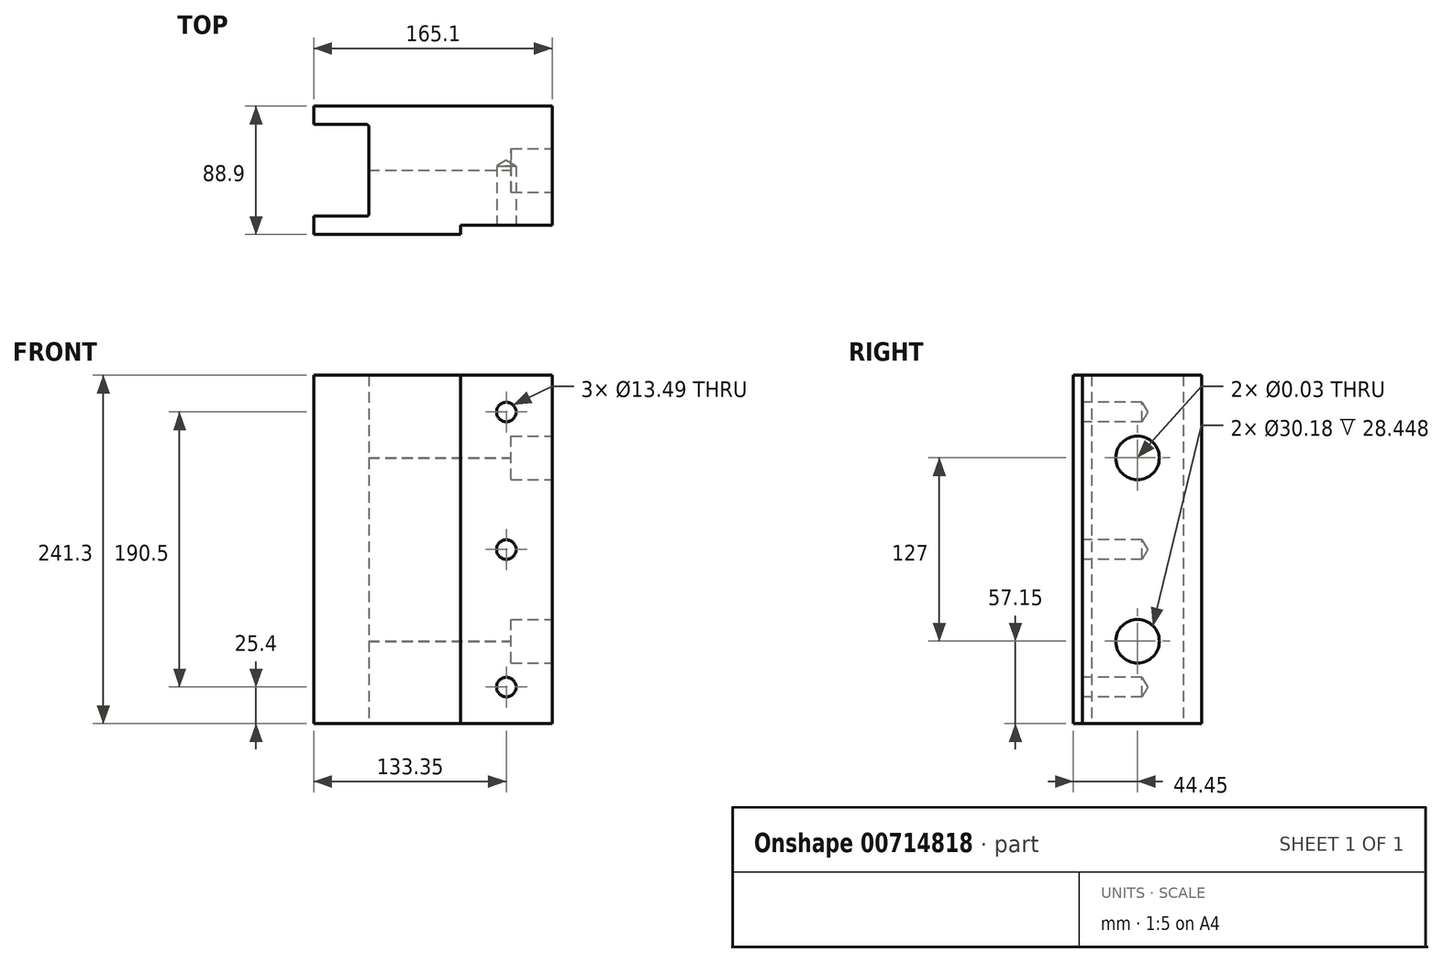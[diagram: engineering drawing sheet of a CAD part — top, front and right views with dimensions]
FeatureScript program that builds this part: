
annotation { "Feature Type Name" : "Feature", "Feature Type Description" : "" }
export const myFeature = defineFeature(function(context is Context, id is Id, definition is map)
    precondition{}
    {
        {
            var Q0;
            Q0=qCreatedBy(makeId("Top.planeOp"),FACE);
            var sketch = newSketch(context, id + "F0", { "sketchPlane" : qUnion([Q0])});
            skLineSegment(sketch, "E0.bottom", {"start": v(-82.55, 44.45) * mm, "end": v(82.55, 44.45) * mm});
            skLineSegment(sketch, "E0.top", {"start": v(-82.55, -44.45) * mm, "end": v(82.55, -44.45) * mm});
            skLineSegment(sketch, "E0.left", {"start": v(-82.55, 44.45) * mm, "end": v(-82.55, 31.75) * mm});
            skLineSegment(sketch, "E0.right", {"start": v(82.55, 44.45) * mm, "end": v(82.55, -44.45) * mm});
            skPoint(sketch, "E0.middle", {"position": v(0, 0) * mm});
            skLineSegment(sketch, "E1.bottom", {"start": v(-44.45, -31.75) * mm, "end": v(-120.65, -31.75) * mm});
            skLineSegment(sketch, "E1.top", {"start": v(-44.45, 31.75) * mm, "end": v(-120.65, 31.75) * mm});
            skLineSegment(sketch, "E1.left", {"start": v(-44.45, -31.75) * mm, "end": v(-44.45, 31.75) * mm});
            skPoint(sketch, "E1.middle", {"position": v(-82.55, 0) * mm});
            skLineSegment(sketch, "E2.trimOffspring", {"start": v(-82.55, 0) * mm, "end": v(-82.55, -44.45) * mm});
            skSolve(sketch);
        }
        {
            var Q0;
            Q0=qSketchRegion(id+"F0",true);
            extrude(context, id + "F1", {"entities" : qUnion([Q0]), "endBound" : BoundingType.SYMMETRIC, "depth" : 241.3 * mm, "offsetDistance" : 25.4 * mm});
        }
        {
            var Q0;
            Q0=makeQuery(id+"F1.opExtrude","SWEPT_EDGE",EDGE,{"disambiguationData":[OSD([sQuery(id+"F0.wireOp",EDGE,"E1.top"),sQuery(id+"F0.wireOp",EDGE,"E1.left")])]});
            var Q1;
            Q1=makeQuery(id+"F1.opExtrude","SWEPT_EDGE",EDGE,{"disambiguationData":[OSD([sQuery(id+"F0.wireOp",EDGE,"E1.bottom"),sQuery(id+"F0.wireOp",EDGE,"E1.left")])]});
            fillet(context, id + "F2", {"entities" : qUnion([Q0, Q1]), "radius" : 1.52 * mm, "tangentPropagation" : true, "allowEdgeOverflow" : false});
        }
        {
            var Q0;
            Q0=makeQuery(id+"F1.opExtrude","SWEPT_FACE",FACE,{"disambiguationData":[OSD([sQuery(id+"F0.wireOp",EDGE,"E0.right")])]});
            var sketch = newSketch(context, id + "F3", { "sketchPlane" : qUnion([Q0])});
            skLineSegment(sketch, "E3", {"start": v(0, -145.44) * mm, "end": v(0, 141.68) * mm, "construction": true});
            skLineSegment(sketch, "E4.0", {"start": v(44.45, -120.65) * mm, "end": v(-44.45, -120.65) * mm, "construction": true});
            skLineSegment(sketch, "E5.0", {"start": v(44.45, -63.5) * mm, "end": v(-44.45, -63.5) * mm, "construction": true});
            skLineSegment(sketch, "E6.0", {"start": v(44.45, 63.5) * mm, "end": v(-44.45, 63.5) * mm, "construction": true});
            skPoint(sketch, "E7", {"position": v(0, 63.5) * mm});
            skPoint(sketch, "E8", {"position": v(0, -63.5) * mm});
            skSolve(sketch);
        }
        {
            var Q0;
            Q0=sQuery(id+"F3.wireOp",VERTEX,"E7");
            var Q1;
            Q1=sQuery(id+"F3.wireOp",VERTEX,"E8");
            var Q2;
            Q2=makeQuery(id+"F1.opExtrude","SWEPT_BODY",BODY,{"disambiguationData":[OSD([sQuery(id+"F0.wireOp",EDGE,"E0.bottom"),sQuery(id+"F0.wireOp",EDGE,"E0.top"),sQuery(id+"F0.wireOp",EDGE,"E0.left"),sQuery(id+"F0.wireOp",EDGE,"E0.right"),sQuery(id+"F0.wireOp",EDGE,"E1.bottom"),sQuery(id+"F0.wireOp",EDGE,"E1.top"),sQuery(id+"F0.wireOp",EDGE,"E1.left"),sQuery(id+"F0.wireOp",EDGE,"E2.trimOffspring")])]});
            hole(context, id + "F4", {"style" : HoleStyle.C_BORE, "endStyle" : HoleEndStyle.THROUGH, "standardTappedOrClearance" : lookupTablePath({ "standard" : "ANSI", "size" : "13/16 (0.81)", "type" : "Drilled" }), "standardBlindInLast" : lookupTablePath({ "standard" : "ANSI", "size" : "13/16", "type" : "Drilled" }), "holeDiameter" : 13 / 406.4 * mm, "cBoreDiameter" : 30.18 * mm, "cBoreDepth" : 28.45 * mm, "majorDiameter" : 6.35 * mm, "isTappedThrough" : true, "tappedDepth" : 34.3 * mm, "tapClearance" : 3, "locations" : qUnion([Q0, Q1]), "scope" : qUnion([Q2])});
        }
        {
            var Q0;
            Q0=makeQuery(id+"F1.opExtrude","SWEPT_FACE",FACE,{"disambiguationData":[OSD([sQuery(id+"F0.wireOp",EDGE,"E0.top")])]});
            var sketch = newSketch(context, id + "F5", { "sketchPlane" : qUnion([Q0])});
            skLineSegment(sketch, "E9.bottom", {"start": v(82.55, 120.65) * mm, "end": v(19.05, 120.65) * mm});
            skLineSegment(sketch, "E9.top", {"start": v(82.55, -120.65) * mm, "end": v(19.05, -120.65) * mm});
            skLineSegment(sketch, "E9.left", {"start": v(82.55, 120.65) * mm, "end": v(82.55, -120.65) * mm});
            skLineSegment(sketch, "E9.right", {"start": v(19.05, 120.65) * mm, "end": v(19.05, -120.65) * mm});
            skSolve(sketch);
        }
        {
            var Q0;
            Q0=qSketchRegion(id+"F5",true);
            extrude(context, id + "F6", {"entities" : qUnion([Q0]), "operationType" : NewBodyOperationType.REMOVE, "oppositeDirection" : true, "depth" : 6.35 * mm, "offsetDistance" : 25.4 * mm});
        }
        {
            var Q0;
            Q0=makeQuery(id+"F6.boolean.opBoolean","COPY",FACE,{"derivedFrom":makeQuery(id+"F6.opExtrude","CAP_FACE",FACE,{"disambiguationData":[OSD([sQuery(id+"F5.wireOp",EDGE,"E9.bottom"),sQuery(id+"F5.wireOp",EDGE,"E9.top"),sQuery(id+"F5.wireOp",EDGE,"E9.left"),sQuery(id+"F5.wireOp",EDGE,"E9.right")])],"isStart":false})});
            var sketch = newSketch(context, id + "F7", { "sketchPlane" : qUnion([Q0])});
            skLineSegment(sketch, "E10.0", {"start": v(82.55, 120.65) * mm, "end": v(82.55, -120.65) * mm, "construction": true});
            skLineSegment(sketch, "E11", {"start": v(173.2, 0) * mm, "end": v(-136.03, 0) * mm, "construction": true});
            skLineSegment(sketch, "E12.0", {"start": v(50.8, 120.65) * mm, "end": v(50.8, -120.65) * mm, "construction": true});
            skLineSegment(sketch, "E13.0", {"start": v(173.2, 95.25) * mm, "end": v(-136.03, 95.25) * mm, "construction": true});
            skPoint(sketch, "E14", {"position": v(50.8, 95.25) * mm});
            skPoint(sketch, "E15", {"position": v(50.8, 0) * mm});
            skPoint(sketch, "E16.MirrorP", {"position": v(50.8, -95.25) * mm});
            skSolve(sketch);
        }
        {
            var Q0;
            Q0=sQuery(id+"F7.wireOp",VERTEX,"E14");
            var Q1;
            Q1=sQuery(id+"F7.wireOp",VERTEX,"E15");
            var Q2;
            Q2=sQuery(id+"F7.wireOp",VERTEX,"E16.MirrorP");
            var Q3;
            Q3=makeQuery(id+"F1.opExtrude","SWEPT_BODY",BODY,{"disambiguationData":[OSD([sQuery(id+"F0.wireOp",EDGE,"E0.bottom"),sQuery(id+"F0.wireOp",EDGE,"E0.top"),sQuery(id+"F0.wireOp",EDGE,"E0.left"),sQuery(id+"F0.wireOp",EDGE,"E0.right"),sQuery(id+"F0.wireOp",EDGE,"E1.bottom"),sQuery(id+"F0.wireOp",EDGE,"E1.top"),sQuery(id+"F0.wireOp",EDGE,"E1.left"),sQuery(id+"F0.wireOp",EDGE,"E2.trimOffspring")])]});
            hole(context, id + "F8", {"style" : HoleStyle.SIMPLE, "endStyle" : HoleEndStyle.BLIND, "standardTappedOrClearance" : lookupTablePath({ "standard" : "ANSI", "engagement" : "75%", "pitch" : "11 tpi", "size" : "5/8", "type" : "Tapped" }), "standardBlindInLast" : lookupTablePath({ "standard" : "ANSI", "engagement" : "75%", "pitch" : "11 tpi", "size" : "5/8", "type" : "Tapped" }), "holeDiameter" : 13.5 * mm, "majorDiameter" : 15.88 * mm, "showTappedDepth" : true, "holeDepth" : 41.22 * mm, "isTappedThrough" : true, "tappedDepth" : 34.3 * mm, "tapClearance" : 3, "locations" : qUnion([Q0, Q1, Q2]), "scope" : qUnion([Q3])});
        }
    });
